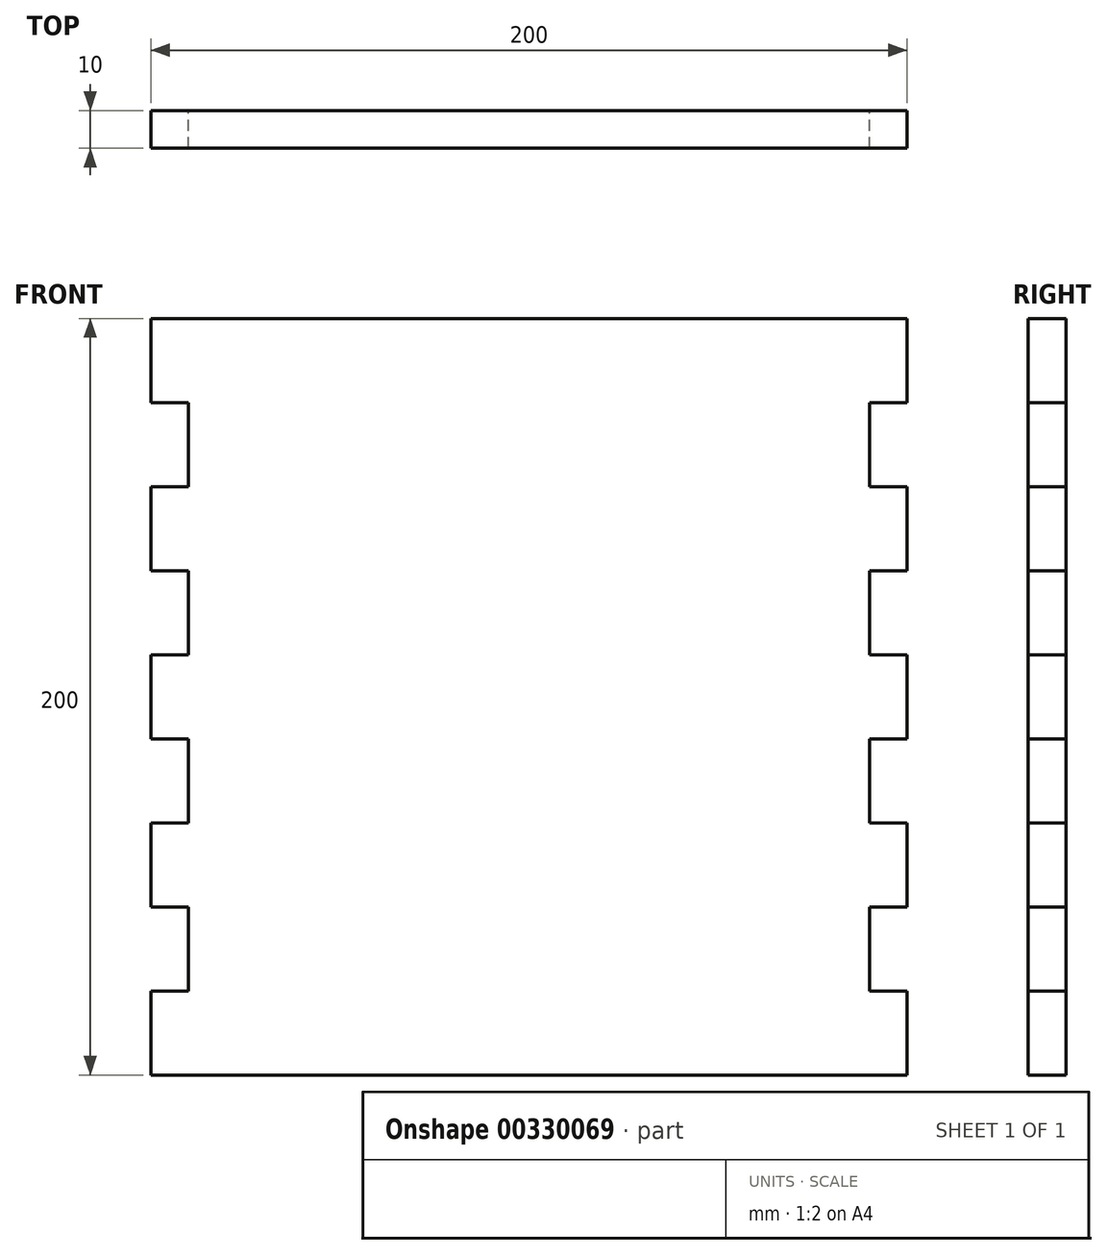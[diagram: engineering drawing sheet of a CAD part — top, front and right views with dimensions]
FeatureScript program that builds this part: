
annotation { "Feature Type Name" : "Feature", "Feature Type Description" : "" }
export const myFeature = defineFeature(function(context is Context, id is Id, definition is map)
    precondition{}
    {
        {
            var Q0;
            Q0=qCreatedBy(makeId("Front.planeOp"),FACE);
            var sketch = newSketch(context, id + "F0", { "sketchPlane" : qUnion([Q0])});
            skLineSegment(sketch, "E0.bottom", {"start": v(-185.33, 226.05) * mm, "end": v(14.67, 226.05) * mm});
            skLineSegment(sketch, "E0.left", {"start": v(-185.33, 226.05) * mm, "end": v(-185.33, 203.83) * mm});
            skLineSegment(sketch, "E0.right", {"start": v(14.67, 226.05) * mm, "end": v(14.67, 203.83) * mm});
            skLineSegment(sketch, "E1", {"start": v(-175.33, 203.83) * mm, "end": v(-175.33, 181.6) * mm});
            skLineSegment(sketch, "E2", {"start": v(4.67, 203.83) * mm, "end": v(4.67, 181.6) * mm});
            skLineSegment(sketch, "E3", {"start": v(-185.33, 203.83) * mm, "end": v(-175.33, 203.83) * mm});
            skLineSegment(sketch, "E4", {"start": v(-185.33, 181.6) * mm, "end": v(-175.33, 181.6) * mm});
            skLineSegment(sketch, "E5", {"start": v(-185.33, 159.39) * mm, "end": v(-175.33, 159.39) * mm});
            skLineSegment(sketch, "E6", {"start": v(-185.33, 114.94) * mm, "end": v(-175.33, 114.94) * mm});
            skLineSegment(sketch, "E7", {"start": v(-185.33, 137.16) * mm, "end": v(-175.33, 137.16) * mm});
            skLineSegment(sketch, "E8", {"start": v(-185.33, 70.5) * mm, "end": v(-175.33, 70.5) * mm});
            skLineSegment(sketch, "E9", {"start": v(-185.33, 48.28) * mm, "end": v(-175.33, 48.28) * mm});
            skLineSegment(sketch, "E10", {"start": v(-185.33, 26.05) * mm, "end": v(-175.33, 26.05) * mm});
            skLineSegment(sketch, "E11", {"start": v(-185.33, 92.72) * mm, "end": v(-175.33, 92.72) * mm});
            skLineSegment(sketch, "E12.trimOffspring", {"start": v(-185.33, 181.6) * mm, "end": v(-185.33, 159.39) * mm});
            skLineSegment(sketch, "E13.trimOffspring", {"start": v(-185.33, 137.16) * mm, "end": v(-185.33, 114.94) * mm});
            skLineSegment(sketch, "E14.trimOffspring", {"start": v(-185.33, 92.72) * mm, "end": v(-185.33, 70.5) * mm});
            skLineSegment(sketch, "E15.trimOffspring", {"start": v(-185.33, 48.28) * mm, "end": v(-185.33, 26.05) * mm});
            skLineSegment(sketch, "E16", {"start": v(-175.33, 26.05) * mm, "end": v(14.67, 26.05) * mm});
            skLineSegment(sketch, "E17", {"start": v(4.67, 203.83) * mm, "end": v(14.67, 203.83) * mm});
            skLineSegment(sketch, "E18", {"start": v(4.67, 181.6) * mm, "end": v(14.67, 181.6) * mm});
            skLineSegment(sketch, "E19", {"start": v(4.67, 159.39) * mm, "end": v(14.67, 159.39) * mm});
            skLineSegment(sketch, "E20", {"start": v(4.67, 114.94) * mm, "end": v(14.67, 114.94) * mm});
            skLineSegment(sketch, "E21", {"start": v(4.67, 137.16) * mm, "end": v(14.67, 137.16) * mm});
            skLineSegment(sketch, "E22", {"start": v(4.67, 70.5) * mm, "end": v(14.67, 70.5) * mm});
            skLineSegment(sketch, "E23", {"start": v(4.67, 48.28) * mm, "end": v(14.67, 48.28) * mm});
            skLineSegment(sketch, "E24", {"start": v(4.67, 92.72) * mm, "end": v(14.67, 92.72) * mm});
            skLineSegment(sketch, "E25.trimOffspring", {"start": v(14.67, 181.6) * mm, "end": v(14.67, 159.39) * mm});
            skLineSegment(sketch, "E26.trimOffspring", {"start": v(14.67, 137.16) * mm, "end": v(14.67, 114.94) * mm});
            skLineSegment(sketch, "E27.trimOffspring", {"start": v(14.67, 92.72) * mm, "end": v(14.67, 70.5) * mm});
            skLineSegment(sketch, "E28.trimOffspring", {"start": v(14.67, 48.28) * mm, "end": v(14.67, 26.05) * mm});
            skLineSegment(sketch, "E29.trimOffspring", {"start": v(-175.33, 159.39) * mm, "end": v(-175.33, 137.16) * mm});
            skLineSegment(sketch, "E30.trimOffspring", {"start": v(-175.33, 114.94) * mm, "end": v(-175.33, 92.72) * mm});
            skLineSegment(sketch, "E31.trimOffspring", {"start": v(-175.33, 70.5) * mm, "end": v(-175.33, 26.05) * mm});
            skLineSegment(sketch, "E32.trimOffspring", {"start": v(4.67, 159.39) * mm, "end": v(4.67, 137.16) * mm});
            skLineSegment(sketch, "E33.trimOffspring", {"start": v(4.67, 114.94) * mm, "end": v(4.67, 92.72) * mm});
            skLineSegment(sketch, "E34.trimOffspring", {"start": v(4.67, 70.5) * mm, "end": v(4.67, 48.28) * mm});
            skSolve(sketch);
        }
        {
            var Q0;
            Q0 = qSketchRegion(id + "F0", true);
            extrude(context, id + "F1", {"entities" : qUnion([Q0]), "depth" : 10 * mm, "offsetDistance" : 25 * mm});
        }
    });
